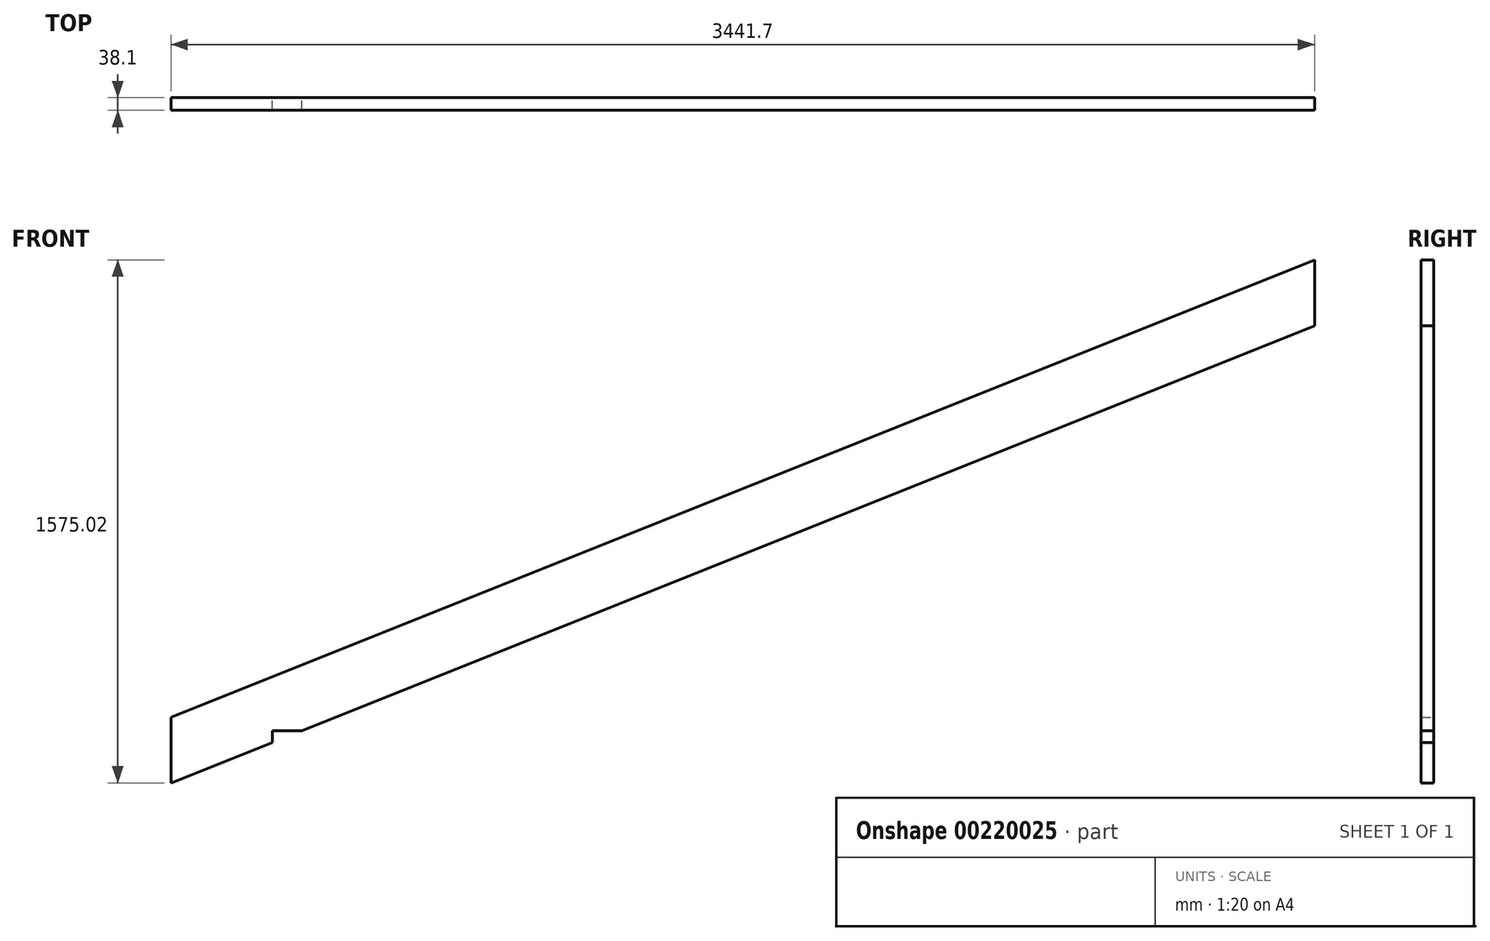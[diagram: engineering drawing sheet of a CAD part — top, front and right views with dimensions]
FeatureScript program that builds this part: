
annotation { "Feature Type Name" : "Feature", "Feature Type Description" : "" }
export const myFeature = defineFeature(function(context is Context, id is Id, definition is map)
    precondition{}
    {
        {
            var Q0;
            Q0=qCreatedBy(makeId("Front.planeOp"),FACE);
            var sketch = newSketch(context, id + "F0", { "sketchPlane" : qUnion([Q0])});
            skLineSegment(sketch, "E0", {"start": v(0, 0) * mm, "end": v(0, 2863.85) * mm, "construction": true});
            skLineSegment(sketch, "E1", {"start": v(0, 2863.85) * mm, "end": v(3048, 4083.05) * mm, "construction": true});
            skLineSegment(sketch, "E2", {"start": v(3048, 4083.05) * mm, "end": v(3048, 0) * mm, "construction": true});
            skLineSegment(sketch, "E3", {"start": v(3048, 0) * mm, "end": v(0, 0) * mm, "construction": true});
            skLineSegment(sketch, "E4", {"start": v(0, 2863.85) * mm, "end": v(-88.9, 2863.85) * mm, "construction": true});
            skLineSegment(sketch, "E5", {"start": v(-88.9, 2863.85) * mm, "end": v(-88.9, 0) * mm, "construction": true});
            skLineSegment(sketch, "E6", {"start": v(-88.9, 0) * mm, "end": v(0, 0) * mm, "construction": true});
            skSolve(sketch);
        }
        {
            var Q0;
            Q0=qCreatedBy(makeId("Front.planeOp"),FACE);
            var sketch = newSketch(context, id + "F1", { "sketchPlane" : qUnion([Q0])});
            skLineSegment(sketch, "E7", {"start": v(3048, 4083.05) * mm, "end": v(0, 2863.85) * mm});
            skLineSegment(sketch, "E8", {"start": v(3048, 4083.05) * mm, "end": v(3048, 4281.39) * mm});
            skLineSegment(sketch, "E9", {"start": v(3048, 4281.39) * mm, "end": v(-393.7, 2904.7) * mm});
            skLineSegment(sketch, "E10", {"start": v(-393.7, 2706.37) * mm, "end": v(-88.9, 2828.29) * mm});
            skLineSegment(sketch, "E11", {"start": v(0, 2863.85) * mm, "end": v(-88.9, 2863.85) * mm});
            skLineSegment(sketch, "E12", {"start": v(-88.9, 2863.85) * mm, "end": v(-88.9, 2828.29) * mm});
            skPoint(sketch, "E13.orphan", {"position": v(0, 2863.85) * mm});
            skLineSegment(sketch, "E14", {"start": v(-393.7, 2706.37) * mm, "end": v(-393.7, 2904.7) * mm});
            skSolve(sketch);
        }
        {
            var Q0;
            Q0=makeQuery(id+"F1.imprint","IMPRINT",FACE,{"disambiguationData":[TD([[makeQuery(id+"F1.imprint","IMPRINT",EDGE,{"derivedFrom":sQuery(id+"F1.wireOp",EDGE,"E7")}),-1.0]])]});
            extrude(context, id + "F2", {"entities" : qUnion([Q0]), "depth" : 38.1 * mm});
        }
    });
